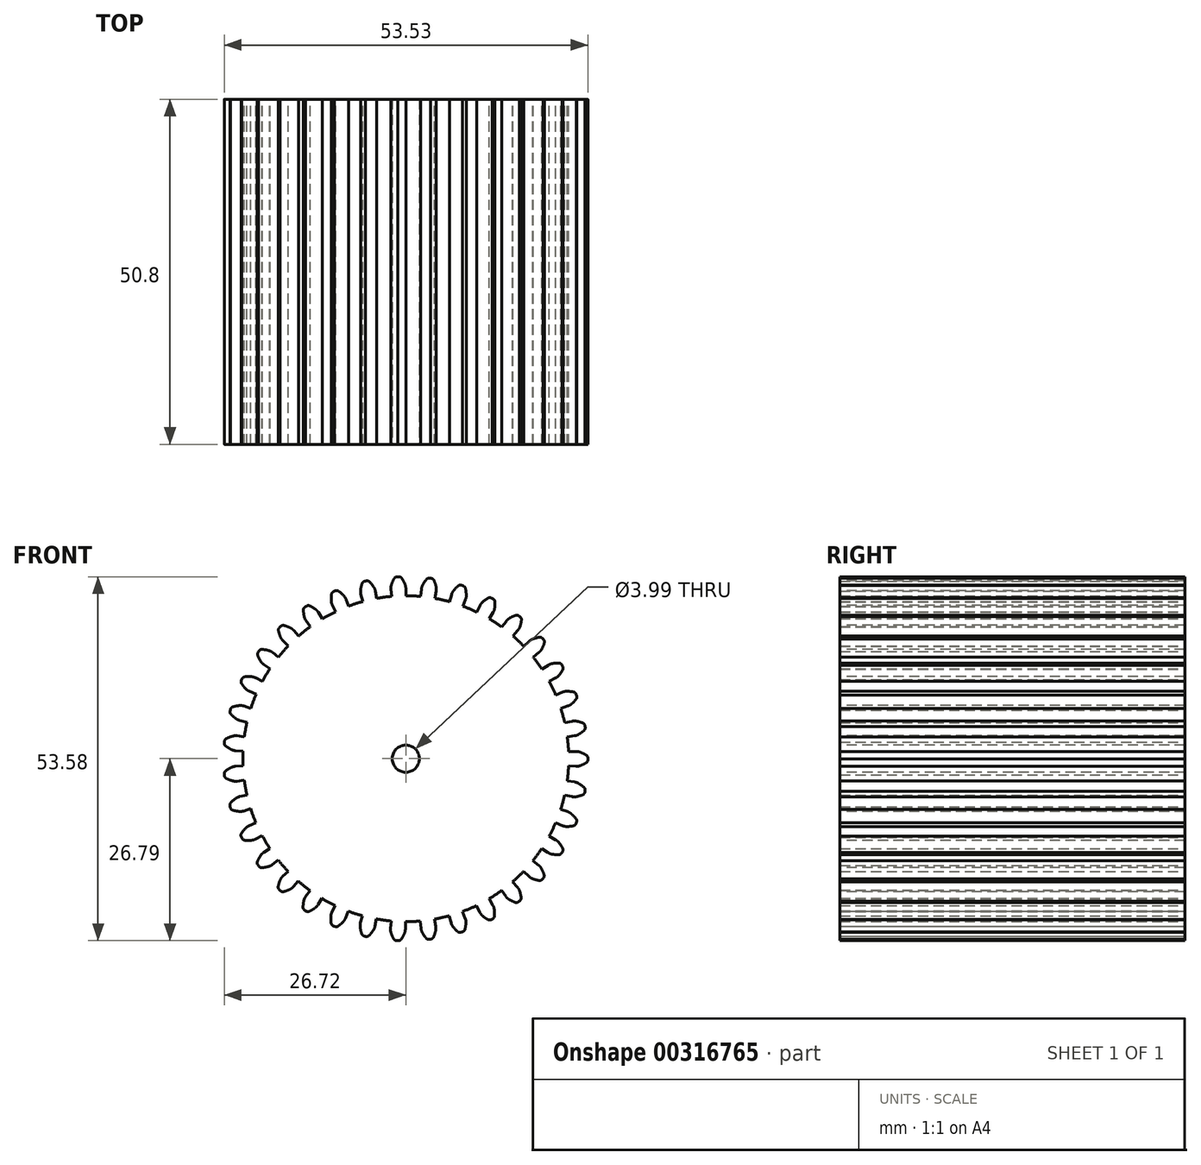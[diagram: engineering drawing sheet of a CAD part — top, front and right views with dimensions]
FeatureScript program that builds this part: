
annotation { "Feature Type Name" : "Feature", "Feature Type Description" : "" }
export const myFeature = defineFeature(function(context is Context, id is Id, definition is map)
    precondition{}
    {
        {
            var Q0;
            Q0=qCreatedBy(makeId("Front.planeOp"),FACE);
            var sketch = newSketch(context, id + "F0", { "sketchPlane" : qUnion([Q0])});
            skCircle(sketch, "E0", {"center": v(0, 0) * mm, "radius": 23.99 * mm});
            skArc(sketch, "E1", {"start": v(-0.14, 25.74) * mm, "mid": v(-0.35, 26.16) * mm, "end": v(-0.59, 26.56) * mm});
            skLineSegment(sketch, "E2", {"start": v(-1.03, 26.8) * mm, "end": v(-1.17, 26.79) * mm});
            skLineSegment(sketch, "E3", {"start": v(0, 25.08) * mm, "end": v(0, 23.99) * mm});
            skLineSegment(sketch, "E4.MirrorCS", {"start": v(-1.3, 26.78) * mm, "end": v(-1.17, 26.79) * mm});
            skArc(sketch, "E5.MirrorCS", {"start": v(-2.1, 25.65) * mm, "mid": v(-1.93, 26.09) * mm, "end": v(-1.73, 26.51) * mm});
            skLineSegment(sketch, "E6.MirrorCS", {"start": v(-2.19, 24.99) * mm, "end": v(-2.1, 23.9) * mm});
            skPoint(sketch, "E7.visualSharp", {"position": v(-2.21, 25.3) * mm});
            skArc(sketch, "E7.filletArc", {"start": v(-2.1, 25.65) * mm, "mid": v(-2.18, 25.32) * mm, "end": v(-2.19, 24.99) * mm});
            skPoint(sketch, "E8.visualSharp", {"position": v(0, 25.4) * mm});
            skArc(sketch, "E8.filletArc", {"start": v(0, 25.08) * mm, "mid": v(-0.04, 25.42) * mm, "end": v(-0.14, 25.74) * mm});
            skPoint(sketch, "E9.visualSharp", {"position": v(-1.59, 26.76) * mm});
            skArc(sketch, "E9.filletArc", {"start": v(-1.3, 26.78) * mm, "mid": v(-1.55, 26.7) * mm, "end": v(-1.73, 26.51) * mm});
            skPoint(sketch, "E10.visualSharp", {"position": v(-0.75, 26.8) * mm});
            skArc(sketch, "E10.filletArc", {"start": v(-0.59, 26.56) * mm, "mid": v(-0.78, 26.73) * mm, "end": v(-1.03, 26.8) * mm});
            skSolve(sketch);
        }
        {
            var Q0;
            Q0=qCreatedBy(makeId("Front.planeOp"),FACE);
            cPlane(context, id + "F1", {"entities" : qUnion([Q0]), "cplaneType" : CPlaneType.OFFSET, "offset" : 50.8 * mm, "width" : 152.4 * mm, "height" : 152.4 * mm});
        }
        {
            var Q0;
            Q0=qCreatedBy(id+"F1.planeOp",FACE);
            var sketch = newSketch(context, id + "F2", { "sketchPlane" : qUnion([Q0])});
            skArc(sketch, "E11.0.0", {"start": v(-2.1, 23.9) * mm, "mid": v(1.05, -23.97) * mm, "end": v(0, 23.99) * mm});
            skArc(sketch, "E11.0.1", {"start": v(0, 23.99) * mm, "mid": v(-1.05, 23.97) * mm, "end": v(-2.1, 23.9) * mm});
            skArc(sketch, "E12.0.0", {"start": v(-1.73, 26.51) * mm, "mid": v(-1.93, 26.09) * mm, "end": v(-2.1, 25.65) * mm});
            skArc(sketch, "E12.0.1", {"start": v(-2.1, 25.65) * mm, "mid": v(-2.18, 25.32) * mm, "end": v(-2.19, 24.99) * mm});
            skLineSegment(sketch, "E12.0.2", {"start": v(-2.19, 24.99) * mm, "end": v(-2.1, 23.9) * mm});
            skArc(sketch, "E12.0.3", {"start": v(-2.1, 23.9) * mm, "mid": v(-1.05, 23.97) * mm, "end": v(0, 23.99) * mm});
            skLineSegment(sketch, "E12.0.4", {"start": v(0, 23.99) * mm, "end": v(0, 25.08) * mm});
            skArc(sketch, "E12.0.5", {"start": v(0, 25.08) * mm, "mid": v(-0.04, 25.42) * mm, "end": v(-0.14, 25.74) * mm});
            skArc(sketch, "E12.0.6", {"start": v(-0.14, 25.74) * mm, "mid": v(-0.35, 26.16) * mm, "end": v(-0.59, 26.56) * mm});
            skArc(sketch, "E12.0.7", {"start": v(-0.59, 26.56) * mm, "mid": v(-0.78, 26.73) * mm, "end": v(-1.03, 26.8) * mm});
            skLineSegment(sketch, "E12.0.8", {"start": v(-1.03, 26.8) * mm, "end": v(-1.17, 26.79) * mm});
            skLineSegment(sketch, "E12.0.9", {"start": v(-1.17, 26.79) * mm, "end": v(-1.3, 26.78) * mm});
            skArc(sketch, "E12.0.10", {"start": v(-1.3, 26.78) * mm, "mid": v(-1.55, 26.7) * mm, "end": v(-1.73, 26.51) * mm});
            skSolve(sketch);
        }
        {
            var Q0;
            Q0=makeQuery(id+"F2.imprint","IMPRINT",FACE,{"disambiguationData":[TD([[makeQuery(id+"F2.imprint","IMPRINT",EDGE,{"derivedFrom":sQuery(id+"F2.wireOp",EDGE,"E12.0.0")}),1.0]])]});
            var Q1;
            Q1=makeQuery(id+"F0.imprint","IMPRINT",FACE,{"disambiguationData":[TD([[makeQuery(id+"F0.imprint","IMPRINT",EDGE,{"derivedFrom":sQuery(id+"F0.wireOp",EDGE,"E1")}),1.0]])]});
            loft(context, id + "F3", {"sheetProfilesArray" : [{ "sheetProfileEntities" : qUnion([Q0]) }, { "sheetProfileEntities" : qUnion([Q1]) }]});
        }
        {
            var Q0;
            Q0=qCreatedBy(makeId("Front.planeOp"),FACE);
            var sketch = newSketch(context, id + "F4", { "sketchPlane" : qUnion([Q0])});
            skCircle(sketch, "E13", {"center": v(0, 0) * mm, "radius": 23.99 * mm});
            skSolve(sketch);
        }
        {
            var Q0;
            Q0=makeQuery(id+"F4.imprint","IMPRINT",FACE,{"disambiguationData":[TD([[makeQuery(id+"F4.imprint","IMPRINT",EDGE,{"derivedFrom":sQuery(id+"F4.wireOp",EDGE,"E13")}),1.0]])]});
            var Q1;
            Q1=makeQuery(id+"F3.opLoft","CAP_FACE",FACE,{"disambiguationData":[OSD([makeQuery(id+"F2.imprint","IMPRINT",FACE,{"disambiguationData":[TD([[makeQuery(id+"F2.imprint","IMPRINT",EDGE,{"derivedFrom":sQuery(id+"F2.wireOp",EDGE,"E12.0.0")}),1.0]])]})])],"isStart":true});
            extrude(context, id + "F5", {"entities" : qUnion([Q0]), "endBound" : BoundingType.UP_TO_SURFACE, "endBoundEntityFace" : qUnion([Q1]), "depth" : 25.4 * mm});
        }
        {
            var Q0;
            Q0=makeQuery(id+"F3.opLoft","SWEPT_BODY",BODY,{"disambiguationData":[OSD([makeQuery(id+"F0.imprint","IMPRINT",FACE,{"disambiguationData":[TD([[makeQuery(id+"F0.imprint","IMPRINT",EDGE,{"derivedFrom":sQuery(id+"F0.wireOp",EDGE,"E1")}),1.0]])]}),makeQuery(id+"F2.imprint","IMPRINT",FACE,{"disambiguationData":[TD([[makeQuery(id+"F2.imprint","IMPRINT",EDGE,{"derivedFrom":sQuery(id+"F2.wireOp",EDGE,"E12.0.0")}),1.0]])]})])]});
            var Q1;
            Q1=makeQuery(id+"F5.opExtrude","SWEPT_FACE",FACE,{"disambiguationData":[OSD([sQuery(id+"F4.wireOp",EDGE,"E13")])]});
            circularPattern(context, id + "F6", {"entities" : qUnion([Q0]), "axis" : qUnion([Q1]), "angle" : 360 * degree, "instanceCount" : 35, "equalSpace" : true});
        }
        {
            var Q0;
            Q0=makeQuery(id+"F6.opPattern","COPY",BODY,{"derivedFrom":makeQuery(id+"F3.opLoft","SWEPT_BODY",BODY,{"disambiguationData":[OSD([makeQuery(id+"F0.imprint","IMPRINT",FACE,{"disambiguationData":[TD([[makeQuery(id+"F0.imprint","IMPRINT",EDGE,{"derivedFrom":sQuery(id+"F0.wireOp",EDGE,"E1")}),1.0]])]}),makeQuery(id+"F2.imprint","IMPRINT",FACE,{"disambiguationData":[TD([[makeQuery(id+"F2.imprint","IMPRINT",EDGE,{"derivedFrom":sQuery(id+"F2.wireOp",EDGE,"E12.0.0")}),1.0]])]})])]}),"instanceName":"1"});
            var Q1;
            Q1=makeQuery(id+"F5.opExtrude","SWEPT_BODY",BODY,{"disambiguationData":[OSD([sQuery(id+"F4.wireOp",EDGE,"E13")])]});
            var Q2;
            Q2=makeQuery(id+"F6.opPattern","COPY",BODY,{"derivedFrom":makeQuery(id+"F3.opLoft","SWEPT_BODY",BODY,{"disambiguationData":[OSD([makeQuery(id+"F0.imprint","IMPRINT",FACE,{"disambiguationData":[TD([[makeQuery(id+"F0.imprint","IMPRINT",EDGE,{"derivedFrom":sQuery(id+"F0.wireOp",EDGE,"E1")}),1.0]])]}),makeQuery(id+"F2.imprint","IMPRINT",FACE,{"disambiguationData":[TD([[makeQuery(id+"F2.imprint","IMPRINT",EDGE,{"derivedFrom":sQuery(id+"F2.wireOp",EDGE,"E12.0.0")}),1.0]])]})])]}),"instanceName":"2"});
            var Q3;
            Q3=makeQuery(id+"F6.opPattern","COPY",BODY,{"derivedFrom":makeQuery(id+"F3.opLoft","SWEPT_BODY",BODY,{"disambiguationData":[OSD([makeQuery(id+"F0.imprint","IMPRINT",FACE,{"disambiguationData":[TD([[makeQuery(id+"F0.imprint","IMPRINT",EDGE,{"derivedFrom":sQuery(id+"F0.wireOp",EDGE,"E1")}),1.0]])]}),makeQuery(id+"F2.imprint","IMPRINT",FACE,{"disambiguationData":[TD([[makeQuery(id+"F2.imprint","IMPRINT",EDGE,{"derivedFrom":sQuery(id+"F2.wireOp",EDGE,"E12.0.0")}),1.0]])]})])]}),"instanceName":"3"});
            var Q4;
            Q4=makeQuery(id+"F6.opPattern","COPY",BODY,{"derivedFrom":makeQuery(id+"F3.opLoft","SWEPT_BODY",BODY,{"disambiguationData":[OSD([makeQuery(id+"F0.imprint","IMPRINT",FACE,{"disambiguationData":[TD([[makeQuery(id+"F0.imprint","IMPRINT",EDGE,{"derivedFrom":sQuery(id+"F0.wireOp",EDGE,"E1")}),1.0]])]}),makeQuery(id+"F2.imprint","IMPRINT",FACE,{"disambiguationData":[TD([[makeQuery(id+"F2.imprint","IMPRINT",EDGE,{"derivedFrom":sQuery(id+"F2.wireOp",EDGE,"E12.0.0")}),1.0]])]})])]}),"instanceName":"4"});
            var Q5;
            Q5=makeQuery(id+"F6.opPattern","COPY",BODY,{"derivedFrom":makeQuery(id+"F3.opLoft","SWEPT_BODY",BODY,{"disambiguationData":[OSD([makeQuery(id+"F0.imprint","IMPRINT",FACE,{"disambiguationData":[TD([[makeQuery(id+"F0.imprint","IMPRINT",EDGE,{"derivedFrom":sQuery(id+"F0.wireOp",EDGE,"E1")}),1.0]])]}),makeQuery(id+"F2.imprint","IMPRINT",FACE,{"disambiguationData":[TD([[makeQuery(id+"F2.imprint","IMPRINT",EDGE,{"derivedFrom":sQuery(id+"F2.wireOp",EDGE,"E12.0.0")}),1.0]])]})])]}),"instanceName":"5"});
            var Q6;
            Q6=makeQuery(id+"F6.opPattern","COPY",BODY,{"derivedFrom":makeQuery(id+"F3.opLoft","SWEPT_BODY",BODY,{"disambiguationData":[OSD([makeQuery(id+"F0.imprint","IMPRINT",FACE,{"disambiguationData":[TD([[makeQuery(id+"F0.imprint","IMPRINT",EDGE,{"derivedFrom":sQuery(id+"F0.wireOp",EDGE,"E1")}),1.0]])]}),makeQuery(id+"F2.imprint","IMPRINT",FACE,{"disambiguationData":[TD([[makeQuery(id+"F2.imprint","IMPRINT",EDGE,{"derivedFrom":sQuery(id+"F2.wireOp",EDGE,"E12.0.0")}),1.0]])]})])]}),"instanceName":"6"});
            var Q7;
            Q7=makeQuery(id+"F6.opPattern","COPY",BODY,{"derivedFrom":makeQuery(id+"F3.opLoft","SWEPT_BODY",BODY,{"disambiguationData":[OSD([makeQuery(id+"F0.imprint","IMPRINT",FACE,{"disambiguationData":[TD([[makeQuery(id+"F0.imprint","IMPRINT",EDGE,{"derivedFrom":sQuery(id+"F0.wireOp",EDGE,"E1")}),1.0]])]}),makeQuery(id+"F2.imprint","IMPRINT",FACE,{"disambiguationData":[TD([[makeQuery(id+"F2.imprint","IMPRINT",EDGE,{"derivedFrom":sQuery(id+"F2.wireOp",EDGE,"E12.0.0")}),1.0]])]})])]}),"instanceName":"7"});
            var Q8;
            Q8=makeQuery(id+"F6.opPattern","COPY",BODY,{"derivedFrom":makeQuery(id+"F3.opLoft","SWEPT_BODY",BODY,{"disambiguationData":[OSD([makeQuery(id+"F0.imprint","IMPRINT",FACE,{"disambiguationData":[TD([[makeQuery(id+"F0.imprint","IMPRINT",EDGE,{"derivedFrom":sQuery(id+"F0.wireOp",EDGE,"E1")}),1.0]])]}),makeQuery(id+"F2.imprint","IMPRINT",FACE,{"disambiguationData":[TD([[makeQuery(id+"F2.imprint","IMPRINT",EDGE,{"derivedFrom":sQuery(id+"F2.wireOp",EDGE,"E12.0.0")}),1.0]])]})])]}),"instanceName":"8"});
            var Q9;
            Q9=makeQuery(id+"F6.opPattern","COPY",BODY,{"derivedFrom":makeQuery(id+"F3.opLoft","SWEPT_BODY",BODY,{"disambiguationData":[OSD([makeQuery(id+"F0.imprint","IMPRINT",FACE,{"disambiguationData":[TD([[makeQuery(id+"F0.imprint","IMPRINT",EDGE,{"derivedFrom":sQuery(id+"F0.wireOp",EDGE,"E1")}),1.0]])]}),makeQuery(id+"F2.imprint","IMPRINT",FACE,{"disambiguationData":[TD([[makeQuery(id+"F2.imprint","IMPRINT",EDGE,{"derivedFrom":sQuery(id+"F2.wireOp",EDGE,"E12.0.0")}),1.0]])]})])]}),"instanceName":"9"});
            var Q10;
            Q10=makeQuery(id+"F6.opPattern","COPY",BODY,{"derivedFrom":makeQuery(id+"F3.opLoft","SWEPT_BODY",BODY,{"disambiguationData":[OSD([makeQuery(id+"F0.imprint","IMPRINT",FACE,{"disambiguationData":[TD([[makeQuery(id+"F0.imprint","IMPRINT",EDGE,{"derivedFrom":sQuery(id+"F0.wireOp",EDGE,"E1")}),1.0]])]}),makeQuery(id+"F2.imprint","IMPRINT",FACE,{"disambiguationData":[TD([[makeQuery(id+"F2.imprint","IMPRINT",EDGE,{"derivedFrom":sQuery(id+"F2.wireOp",EDGE,"E12.0.0")}),1.0]])]})])]}),"instanceName":"10"});
            var Q11;
            Q11=makeQuery(id+"F6.opPattern","COPY",BODY,{"derivedFrom":makeQuery(id+"F3.opLoft","SWEPT_BODY",BODY,{"disambiguationData":[OSD([makeQuery(id+"F0.imprint","IMPRINT",FACE,{"disambiguationData":[TD([[makeQuery(id+"F0.imprint","IMPRINT",EDGE,{"derivedFrom":sQuery(id+"F0.wireOp",EDGE,"E1")}),1.0]])]}),makeQuery(id+"F2.imprint","IMPRINT",FACE,{"disambiguationData":[TD([[makeQuery(id+"F2.imprint","IMPRINT",EDGE,{"derivedFrom":sQuery(id+"F2.wireOp",EDGE,"E12.0.0")}),1.0]])]})])]}),"instanceName":"11"});
            var Q12;
            Q12=makeQuery(id+"F6.opPattern","COPY",BODY,{"derivedFrom":makeQuery(id+"F3.opLoft","SWEPT_BODY",BODY,{"disambiguationData":[OSD([makeQuery(id+"F0.imprint","IMPRINT",FACE,{"disambiguationData":[TD([[makeQuery(id+"F0.imprint","IMPRINT",EDGE,{"derivedFrom":sQuery(id+"F0.wireOp",EDGE,"E1")}),1.0]])]}),makeQuery(id+"F2.imprint","IMPRINT",FACE,{"disambiguationData":[TD([[makeQuery(id+"F2.imprint","IMPRINT",EDGE,{"derivedFrom":sQuery(id+"F2.wireOp",EDGE,"E12.0.0")}),1.0]])]})])]}),"instanceName":"12"});
            var Q13;
            Q13=makeQuery(id+"F6.opPattern","COPY",BODY,{"derivedFrom":makeQuery(id+"F3.opLoft","SWEPT_BODY",BODY,{"disambiguationData":[OSD([makeQuery(id+"F0.imprint","IMPRINT",FACE,{"disambiguationData":[TD([[makeQuery(id+"F0.imprint","IMPRINT",EDGE,{"derivedFrom":sQuery(id+"F0.wireOp",EDGE,"E1")}),1.0]])]}),makeQuery(id+"F2.imprint","IMPRINT",FACE,{"disambiguationData":[TD([[makeQuery(id+"F2.imprint","IMPRINT",EDGE,{"derivedFrom":sQuery(id+"F2.wireOp",EDGE,"E12.0.0")}),1.0]])]})])]}),"instanceName":"13"});
            var Q14;
            Q14=makeQuery(id+"F6.opPattern","COPY",BODY,{"derivedFrom":makeQuery(id+"F3.opLoft","SWEPT_BODY",BODY,{"disambiguationData":[OSD([makeQuery(id+"F0.imprint","IMPRINT",FACE,{"disambiguationData":[TD([[makeQuery(id+"F0.imprint","IMPRINT",EDGE,{"derivedFrom":sQuery(id+"F0.wireOp",EDGE,"E1")}),1.0]])]}),makeQuery(id+"F2.imprint","IMPRINT",FACE,{"disambiguationData":[TD([[makeQuery(id+"F2.imprint","IMPRINT",EDGE,{"derivedFrom":sQuery(id+"F2.wireOp",EDGE,"E12.0.0")}),1.0]])]})])]}),"instanceName":"14"});
            var Q15;
            Q15=makeQuery(id+"F6.opPattern","COPY",BODY,{"derivedFrom":makeQuery(id+"F3.opLoft","SWEPT_BODY",BODY,{"disambiguationData":[OSD([makeQuery(id+"F0.imprint","IMPRINT",FACE,{"disambiguationData":[TD([[makeQuery(id+"F0.imprint","IMPRINT",EDGE,{"derivedFrom":sQuery(id+"F0.wireOp",EDGE,"E1")}),1.0]])]}),makeQuery(id+"F2.imprint","IMPRINT",FACE,{"disambiguationData":[TD([[makeQuery(id+"F2.imprint","IMPRINT",EDGE,{"derivedFrom":sQuery(id+"F2.wireOp",EDGE,"E12.0.0")}),1.0]])]})])]}),"instanceName":"15"});
            var Q16;
            Q16=makeQuery(id+"F6.opPattern","COPY",BODY,{"derivedFrom":makeQuery(id+"F3.opLoft","SWEPT_BODY",BODY,{"disambiguationData":[OSD([makeQuery(id+"F0.imprint","IMPRINT",FACE,{"disambiguationData":[TD([[makeQuery(id+"F0.imprint","IMPRINT",EDGE,{"derivedFrom":sQuery(id+"F0.wireOp",EDGE,"E1")}),1.0]])]}),makeQuery(id+"F2.imprint","IMPRINT",FACE,{"disambiguationData":[TD([[makeQuery(id+"F2.imprint","IMPRINT",EDGE,{"derivedFrom":sQuery(id+"F2.wireOp",EDGE,"E12.0.0")}),1.0]])]})])]}),"instanceName":"16"});
            var Q17;
            Q17=makeQuery(id+"F6.opPattern","COPY",BODY,{"derivedFrom":makeQuery(id+"F3.opLoft","SWEPT_BODY",BODY,{"disambiguationData":[OSD([makeQuery(id+"F0.imprint","IMPRINT",FACE,{"disambiguationData":[TD([[makeQuery(id+"F0.imprint","IMPRINT",EDGE,{"derivedFrom":sQuery(id+"F0.wireOp",EDGE,"E1")}),1.0]])]}),makeQuery(id+"F2.imprint","IMPRINT",FACE,{"disambiguationData":[TD([[makeQuery(id+"F2.imprint","IMPRINT",EDGE,{"derivedFrom":sQuery(id+"F2.wireOp",EDGE,"E12.0.0")}),1.0]])]})])]}),"instanceName":"17"});
            var Q18;
            Q18=makeQuery(id+"F6.opPattern","COPY",BODY,{"derivedFrom":makeQuery(id+"F3.opLoft","SWEPT_BODY",BODY,{"disambiguationData":[OSD([makeQuery(id+"F0.imprint","IMPRINT",FACE,{"disambiguationData":[TD([[makeQuery(id+"F0.imprint","IMPRINT",EDGE,{"derivedFrom":sQuery(id+"F0.wireOp",EDGE,"E1")}),1.0]])]}),makeQuery(id+"F2.imprint","IMPRINT",FACE,{"disambiguationData":[TD([[makeQuery(id+"F2.imprint","IMPRINT",EDGE,{"derivedFrom":sQuery(id+"F2.wireOp",EDGE,"E12.0.0")}),1.0]])]})])]}),"instanceName":"18"});
            var Q19;
            Q19=makeQuery(id+"F6.opPattern","COPY",BODY,{"derivedFrom":makeQuery(id+"F3.opLoft","SWEPT_BODY",BODY,{"disambiguationData":[OSD([makeQuery(id+"F0.imprint","IMPRINT",FACE,{"disambiguationData":[TD([[makeQuery(id+"F0.imprint","IMPRINT",EDGE,{"derivedFrom":sQuery(id+"F0.wireOp",EDGE,"E1")}),1.0]])]}),makeQuery(id+"F2.imprint","IMPRINT",FACE,{"disambiguationData":[TD([[makeQuery(id+"F2.imprint","IMPRINT",EDGE,{"derivedFrom":sQuery(id+"F2.wireOp",EDGE,"E12.0.0")}),1.0]])]})])]}),"instanceName":"19"});
            var Q20;
            Q20=makeQuery(id+"F6.opPattern","COPY",BODY,{"derivedFrom":makeQuery(id+"F3.opLoft","SWEPT_BODY",BODY,{"disambiguationData":[OSD([makeQuery(id+"F0.imprint","IMPRINT",FACE,{"disambiguationData":[TD([[makeQuery(id+"F0.imprint","IMPRINT",EDGE,{"derivedFrom":sQuery(id+"F0.wireOp",EDGE,"E1")}),1.0]])]}),makeQuery(id+"F2.imprint","IMPRINT",FACE,{"disambiguationData":[TD([[makeQuery(id+"F2.imprint","IMPRINT",EDGE,{"derivedFrom":sQuery(id+"F2.wireOp",EDGE,"E12.0.0")}),1.0]])]})])]}),"instanceName":"20"});
            var Q21;
            Q21=makeQuery(id+"F6.opPattern","COPY",BODY,{"derivedFrom":makeQuery(id+"F3.opLoft","SWEPT_BODY",BODY,{"disambiguationData":[OSD([makeQuery(id+"F0.imprint","IMPRINT",FACE,{"disambiguationData":[TD([[makeQuery(id+"F0.imprint","IMPRINT",EDGE,{"derivedFrom":sQuery(id+"F0.wireOp",EDGE,"E1")}),1.0]])]}),makeQuery(id+"F2.imprint","IMPRINT",FACE,{"disambiguationData":[TD([[makeQuery(id+"F2.imprint","IMPRINT",EDGE,{"derivedFrom":sQuery(id+"F2.wireOp",EDGE,"E12.0.0")}),1.0]])]})])]}),"instanceName":"21"});
            var Q22;
            Q22=makeQuery(id+"F6.opPattern","COPY",BODY,{"derivedFrom":makeQuery(id+"F3.opLoft","SWEPT_BODY",BODY,{"disambiguationData":[OSD([makeQuery(id+"F0.imprint","IMPRINT",FACE,{"disambiguationData":[TD([[makeQuery(id+"F0.imprint","IMPRINT",EDGE,{"derivedFrom":sQuery(id+"F0.wireOp",EDGE,"E1")}),1.0]])]}),makeQuery(id+"F2.imprint","IMPRINT",FACE,{"disambiguationData":[TD([[makeQuery(id+"F2.imprint","IMPRINT",EDGE,{"derivedFrom":sQuery(id+"F2.wireOp",EDGE,"E12.0.0")}),1.0]])]})])]}),"instanceName":"22"});
            var Q23;
            Q23=makeQuery(id+"F6.opPattern","COPY",BODY,{"derivedFrom":makeQuery(id+"F3.opLoft","SWEPT_BODY",BODY,{"disambiguationData":[OSD([makeQuery(id+"F0.imprint","IMPRINT",FACE,{"disambiguationData":[TD([[makeQuery(id+"F0.imprint","IMPRINT",EDGE,{"derivedFrom":sQuery(id+"F0.wireOp",EDGE,"E1")}),1.0]])]}),makeQuery(id+"F2.imprint","IMPRINT",FACE,{"disambiguationData":[TD([[makeQuery(id+"F2.imprint","IMPRINT",EDGE,{"derivedFrom":sQuery(id+"F2.wireOp",EDGE,"E12.0.0")}),1.0]])]})])]}),"instanceName":"23"});
            var Q24;
            Q24=makeQuery(id+"F6.opPattern","COPY",BODY,{"derivedFrom":makeQuery(id+"F3.opLoft","SWEPT_BODY",BODY,{"disambiguationData":[OSD([makeQuery(id+"F0.imprint","IMPRINT",FACE,{"disambiguationData":[TD([[makeQuery(id+"F0.imprint","IMPRINT",EDGE,{"derivedFrom":sQuery(id+"F0.wireOp",EDGE,"E1")}),1.0]])]}),makeQuery(id+"F2.imprint","IMPRINT",FACE,{"disambiguationData":[TD([[makeQuery(id+"F2.imprint","IMPRINT",EDGE,{"derivedFrom":sQuery(id+"F2.wireOp",EDGE,"E12.0.0")}),1.0]])]})])]}),"instanceName":"24"});
            var Q25;
            Q25=makeQuery(id+"F6.opPattern","COPY",BODY,{"derivedFrom":makeQuery(id+"F3.opLoft","SWEPT_BODY",BODY,{"disambiguationData":[OSD([makeQuery(id+"F0.imprint","IMPRINT",FACE,{"disambiguationData":[TD([[makeQuery(id+"F0.imprint","IMPRINT",EDGE,{"derivedFrom":sQuery(id+"F0.wireOp",EDGE,"E1")}),1.0]])]}),makeQuery(id+"F2.imprint","IMPRINT",FACE,{"disambiguationData":[TD([[makeQuery(id+"F2.imprint","IMPRINT",EDGE,{"derivedFrom":sQuery(id+"F2.wireOp",EDGE,"E12.0.0")}),1.0]])]})])]}),"instanceName":"25"});
            var Q26;
            Q26=makeQuery(id+"F6.opPattern","COPY",BODY,{"derivedFrom":makeQuery(id+"F3.opLoft","SWEPT_BODY",BODY,{"disambiguationData":[OSD([makeQuery(id+"F0.imprint","IMPRINT",FACE,{"disambiguationData":[TD([[makeQuery(id+"F0.imprint","IMPRINT",EDGE,{"derivedFrom":sQuery(id+"F0.wireOp",EDGE,"E1")}),1.0]])]}),makeQuery(id+"F2.imprint","IMPRINT",FACE,{"disambiguationData":[TD([[makeQuery(id+"F2.imprint","IMPRINT",EDGE,{"derivedFrom":sQuery(id+"F2.wireOp",EDGE,"E12.0.0")}),1.0]])]})])]}),"instanceName":"26"});
            var Q27;
            Q27=makeQuery(id+"F6.opPattern","COPY",BODY,{"derivedFrom":makeQuery(id+"F3.opLoft","SWEPT_BODY",BODY,{"disambiguationData":[OSD([makeQuery(id+"F0.imprint","IMPRINT",FACE,{"disambiguationData":[TD([[makeQuery(id+"F0.imprint","IMPRINT",EDGE,{"derivedFrom":sQuery(id+"F0.wireOp",EDGE,"E1")}),1.0]])]}),makeQuery(id+"F2.imprint","IMPRINT",FACE,{"disambiguationData":[TD([[makeQuery(id+"F2.imprint","IMPRINT",EDGE,{"derivedFrom":sQuery(id+"F2.wireOp",EDGE,"E12.0.0")}),1.0]])]})])]}),"instanceName":"28"});
            var Q28;
            Q28=makeQuery(id+"F6.opPattern","COPY",BODY,{"derivedFrom":makeQuery(id+"F3.opLoft","SWEPT_BODY",BODY,{"disambiguationData":[OSD([makeQuery(id+"F0.imprint","IMPRINT",FACE,{"disambiguationData":[TD([[makeQuery(id+"F0.imprint","IMPRINT",EDGE,{"derivedFrom":sQuery(id+"F0.wireOp",EDGE,"E1")}),1.0]])]}),makeQuery(id+"F2.imprint","IMPRINT",FACE,{"disambiguationData":[TD([[makeQuery(id+"F2.imprint","IMPRINT",EDGE,{"derivedFrom":sQuery(id+"F2.wireOp",EDGE,"E12.0.0")}),1.0]])]})])]}),"instanceName":"27"});
            var Q29;
            Q29=makeQuery(id+"F6.opPattern","COPY",BODY,{"derivedFrom":makeQuery(id+"F3.opLoft","SWEPT_BODY",BODY,{"disambiguationData":[OSD([makeQuery(id+"F0.imprint","IMPRINT",FACE,{"disambiguationData":[TD([[makeQuery(id+"F0.imprint","IMPRINT",EDGE,{"derivedFrom":sQuery(id+"F0.wireOp",EDGE,"E1")}),1.0]])]}),makeQuery(id+"F2.imprint","IMPRINT",FACE,{"disambiguationData":[TD([[makeQuery(id+"F2.imprint","IMPRINT",EDGE,{"derivedFrom":sQuery(id+"F2.wireOp",EDGE,"E12.0.0")}),1.0]])]})])]}),"instanceName":"29"});
            var Q30;
            Q30=makeQuery(id+"F6.opPattern","COPY",BODY,{"derivedFrom":makeQuery(id+"F3.opLoft","SWEPT_BODY",BODY,{"disambiguationData":[OSD([makeQuery(id+"F0.imprint","IMPRINT",FACE,{"disambiguationData":[TD([[makeQuery(id+"F0.imprint","IMPRINT",EDGE,{"derivedFrom":sQuery(id+"F0.wireOp",EDGE,"E1")}),1.0]])]}),makeQuery(id+"F2.imprint","IMPRINT",FACE,{"disambiguationData":[TD([[makeQuery(id+"F2.imprint","IMPRINT",EDGE,{"derivedFrom":sQuery(id+"F2.wireOp",EDGE,"E12.0.0")}),1.0]])]})])]}),"instanceName":"30"});
            var Q31;
            Q31=makeQuery(id+"F6.opPattern","COPY",BODY,{"derivedFrom":makeQuery(id+"F3.opLoft","SWEPT_BODY",BODY,{"disambiguationData":[OSD([makeQuery(id+"F0.imprint","IMPRINT",FACE,{"disambiguationData":[TD([[makeQuery(id+"F0.imprint","IMPRINT",EDGE,{"derivedFrom":sQuery(id+"F0.wireOp",EDGE,"E1")}),1.0]])]}),makeQuery(id+"F2.imprint","IMPRINT",FACE,{"disambiguationData":[TD([[makeQuery(id+"F2.imprint","IMPRINT",EDGE,{"derivedFrom":sQuery(id+"F2.wireOp",EDGE,"E12.0.0")}),1.0]])]})])]}),"instanceName":"31"});
            var Q32;
            Q32=makeQuery(id+"F6.opPattern","COPY",BODY,{"derivedFrom":makeQuery(id+"F3.opLoft","SWEPT_BODY",BODY,{"disambiguationData":[OSD([makeQuery(id+"F0.imprint","IMPRINT",FACE,{"disambiguationData":[TD([[makeQuery(id+"F0.imprint","IMPRINT",EDGE,{"derivedFrom":sQuery(id+"F0.wireOp",EDGE,"E1")}),1.0]])]}),makeQuery(id+"F2.imprint","IMPRINT",FACE,{"disambiguationData":[TD([[makeQuery(id+"F2.imprint","IMPRINT",EDGE,{"derivedFrom":sQuery(id+"F2.wireOp",EDGE,"E12.0.0")}),1.0]])]})])]}),"instanceName":"32"});
            var Q33;
            Q33=makeQuery(id+"F6.opPattern","COPY",BODY,{"derivedFrom":makeQuery(id+"F3.opLoft","SWEPT_BODY",BODY,{"disambiguationData":[OSD([makeQuery(id+"F0.imprint","IMPRINT",FACE,{"disambiguationData":[TD([[makeQuery(id+"F0.imprint","IMPRINT",EDGE,{"derivedFrom":sQuery(id+"F0.wireOp",EDGE,"E1")}),1.0]])]}),makeQuery(id+"F2.imprint","IMPRINT",FACE,{"disambiguationData":[TD([[makeQuery(id+"F2.imprint","IMPRINT",EDGE,{"derivedFrom":sQuery(id+"F2.wireOp",EDGE,"E12.0.0")}),1.0]])]})])]}),"instanceName":"33"});
            var Q34;
            Q34=makeQuery(id+"F6.opPattern","COPY",BODY,{"derivedFrom":makeQuery(id+"F3.opLoft","SWEPT_BODY",BODY,{"disambiguationData":[OSD([makeQuery(id+"F0.imprint","IMPRINT",FACE,{"disambiguationData":[TD([[makeQuery(id+"F0.imprint","IMPRINT",EDGE,{"derivedFrom":sQuery(id+"F0.wireOp",EDGE,"E1")}),1.0]])]}),makeQuery(id+"F2.imprint","IMPRINT",FACE,{"disambiguationData":[TD([[makeQuery(id+"F2.imprint","IMPRINT",EDGE,{"derivedFrom":sQuery(id+"F2.wireOp",EDGE,"E12.0.0")}),1.0]])]})])]}),"instanceName":"34"});
            var Q35;
            Q35=makeQuery(id+"F3.opLoft","SWEPT_BODY",BODY,{"disambiguationData":[OSD([makeQuery(id+"F0.imprint","IMPRINT",FACE,{"disambiguationData":[TD([[makeQuery(id+"F0.imprint","IMPRINT",EDGE,{"derivedFrom":sQuery(id+"F0.wireOp",EDGE,"E1")}),1.0]])]}),makeQuery(id+"F2.imprint","IMPRINT",FACE,{"disambiguationData":[TD([[makeQuery(id+"F2.imprint","IMPRINT",EDGE,{"derivedFrom":sQuery(id+"F2.wireOp",EDGE,"E12.0.0")}),1.0]])]})])]});
            booleanBodies(context, id + "F7", {"operationType" : BooleanOperationType.UNION, "tools" : qUnion([Q0, Q1, Q2, Q3, Q4, Q5, Q6, Q7, Q8, Q9, Q10, Q11, Q12, Q13, Q14, Q15, Q16, Q17, Q18, Q19, Q20, Q21, Q22, Q23, Q24, Q25, Q26, Q27, Q28, Q29, Q30, Q31, Q32, Q33, Q34, Q35])});
        }
        {
            var Q0;
            {var subQ0=makeQuery(id+"F2.imprint","IMPRINT",FACE,{"disambiguationData":[TD([[makeQuery(id+"F2.imprint","IMPRINT",EDGE,{"derivedFrom":sQuery(id+"F2.wireOp",EDGE,"E12.0.0")}),1.0]])]});var subQ1=makeQuery(id+"F3.opLoft","CAP_FACE",FACE,{"disambiguationData":[OSD([subQ0])],"isStart":true});Q0=makeQuery(id+"F7.opBoolean","MERGE",FACE,{"derivedFrom":[subQ1,makeQuery(id+"F5.opExtrude","CAP_FACE",FACE,{"disambiguationData":[OSD([subQ0])],"isStart":false}),makeQuery(id+"F6.opPattern","COPY",FACE,{"derivedFrom":subQ1,"instanceName":"1"}),makeQuery(id+"F6.opPattern","COPY",FACE,{"derivedFrom":subQ1,"instanceName":"2"}),makeQuery(id+"F6.opPattern","COPY",FACE,{"derivedFrom":subQ1,"instanceName":"3"}),makeQuery(id+"F6.opPattern","COPY",FACE,{"derivedFrom":subQ1,"instanceName":"4"}),makeQuery(id+"F6.opPattern","COPY",FACE,{"derivedFrom":subQ1,"instanceName":"5"}),makeQuery(id+"F6.opPattern","COPY",FACE,{"derivedFrom":subQ1,"instanceName":"6"}),makeQuery(id+"F6.opPattern","COPY",FACE,{"derivedFrom":subQ1,"instanceName":"7"}),makeQuery(id+"F6.opPattern","COPY",FACE,{"derivedFrom":subQ1,"instanceName":"8"}),makeQuery(id+"F6.opPattern","COPY",FACE,{"derivedFrom":subQ1,"instanceName":"9"}),makeQuery(id+"F6.opPattern","COPY",FACE,{"derivedFrom":subQ1,"instanceName":"10"}),makeQuery(id+"F6.opPattern","COPY",FACE,{"derivedFrom":subQ1,"instanceName":"11"}),makeQuery(id+"F6.opPattern","COPY",FACE,{"derivedFrom":subQ1,"instanceName":"12"}),makeQuery(id+"F6.opPattern","COPY",FACE,{"derivedFrom":subQ1,"instanceName":"13"}),makeQuery(id+"F6.opPattern","COPY",FACE,{"derivedFrom":subQ1,"instanceName":"14"}),makeQuery(id+"F6.opPattern","COPY",FACE,{"derivedFrom":subQ1,"instanceName":"15"}),makeQuery(id+"F6.opPattern","COPY",FACE,{"derivedFrom":subQ1,"instanceName":"16"}),makeQuery(id+"F6.opPattern","COPY",FACE,{"derivedFrom":subQ1,"instanceName":"17"}),makeQuery(id+"F6.opPattern","COPY",FACE,{"derivedFrom":subQ1,"instanceName":"18"}),makeQuery(id+"F6.opPattern","COPY",FACE,{"derivedFrom":subQ1,"instanceName":"19"}),makeQuery(id+"F6.opPattern","COPY",FACE,{"derivedFrom":subQ1,"instanceName":"20"}),makeQuery(id+"F6.opPattern","COPY",FACE,{"derivedFrom":subQ1,"instanceName":"21"}),makeQuery(id+"F6.opPattern","COPY",FACE,{"derivedFrom":subQ1,"instanceName":"22"}),makeQuery(id+"F6.opPattern","COPY",FACE,{"derivedFrom":subQ1,"instanceName":"23"}),makeQuery(id+"F6.opPattern","COPY",FACE,{"derivedFrom":subQ1,"instanceName":"24"}),makeQuery(id+"F6.opPattern","COPY",FACE,{"derivedFrom":subQ1,"instanceName":"25"}),makeQuery(id+"F6.opPattern","COPY",FACE,{"derivedFrom":subQ1,"instanceName":"26"}),makeQuery(id+"F6.opPattern","COPY",FACE,{"derivedFrom":subQ1,"instanceName":"27"}),makeQuery(id+"F6.opPattern","COPY",FACE,{"derivedFrom":subQ1,"instanceName":"28"}),makeQuery(id+"F6.opPattern","COPY",FACE,{"derivedFrom":subQ1,"instanceName":"29"}),makeQuery(id+"F6.opPattern","COPY",FACE,{"derivedFrom":subQ1,"instanceName":"30"}),makeQuery(id+"F6.opPattern","COPY",FACE,{"derivedFrom":subQ1,"instanceName":"31"}),makeQuery(id+"F6.opPattern","COPY",FACE,{"derivedFrom":subQ1,"instanceName":"32"}),makeQuery(id+"F6.opPattern","COPY",FACE,{"derivedFrom":subQ1,"instanceName":"33"}),makeQuery(id+"F6.opPattern","COPY",FACE,{"derivedFrom":subQ1,"instanceName":"34"})]});}
            var sketch = newSketch(context, id + "F8", { "sketchPlane" : qUnion([Q0])});
            skPoint(sketch, "E14", {"position": v(0, 0) * mm});
            skSolve(sketch);
        }
        {
            var Q0;
            Q0=sQuery(id+"F8.wireOp",VERTEX,"E14");
            var Q1;
            Q1=makeQuery(id+"F6.opPattern","COPY",BODY,{"derivedFrom":makeQuery(id+"F3.opLoft","SWEPT_BODY",BODY,{"disambiguationData":[OSD([makeQuery(id+"F0.imprint","IMPRINT",FACE,{"disambiguationData":[TD([[makeQuery(id+"F0.imprint","IMPRINT",EDGE,{"derivedFrom":sQuery(id+"F0.wireOp",EDGE,"E1")}),1.0]])]}),makeQuery(id+"F2.imprint","IMPRINT",FACE,{"disambiguationData":[TD([[makeQuery(id+"F2.imprint","IMPRINT",EDGE,{"derivedFrom":sQuery(id+"F2.wireOp",EDGE,"E12.0.0")}),1.0]])]})])]}),"instanceName":"1"});
            hole(context, id + "F9", {"style" : HoleStyle.SIMPLE, "endStyle" : HoleEndStyle.THROUGH, "holeDiameter" : 4 * mm, "tappedDepth" : 12.7 * mm, "tapClearance" : 3, "locations" : qUnion([Q0]), "scope" : qUnion([Q1])});
        }
    });
